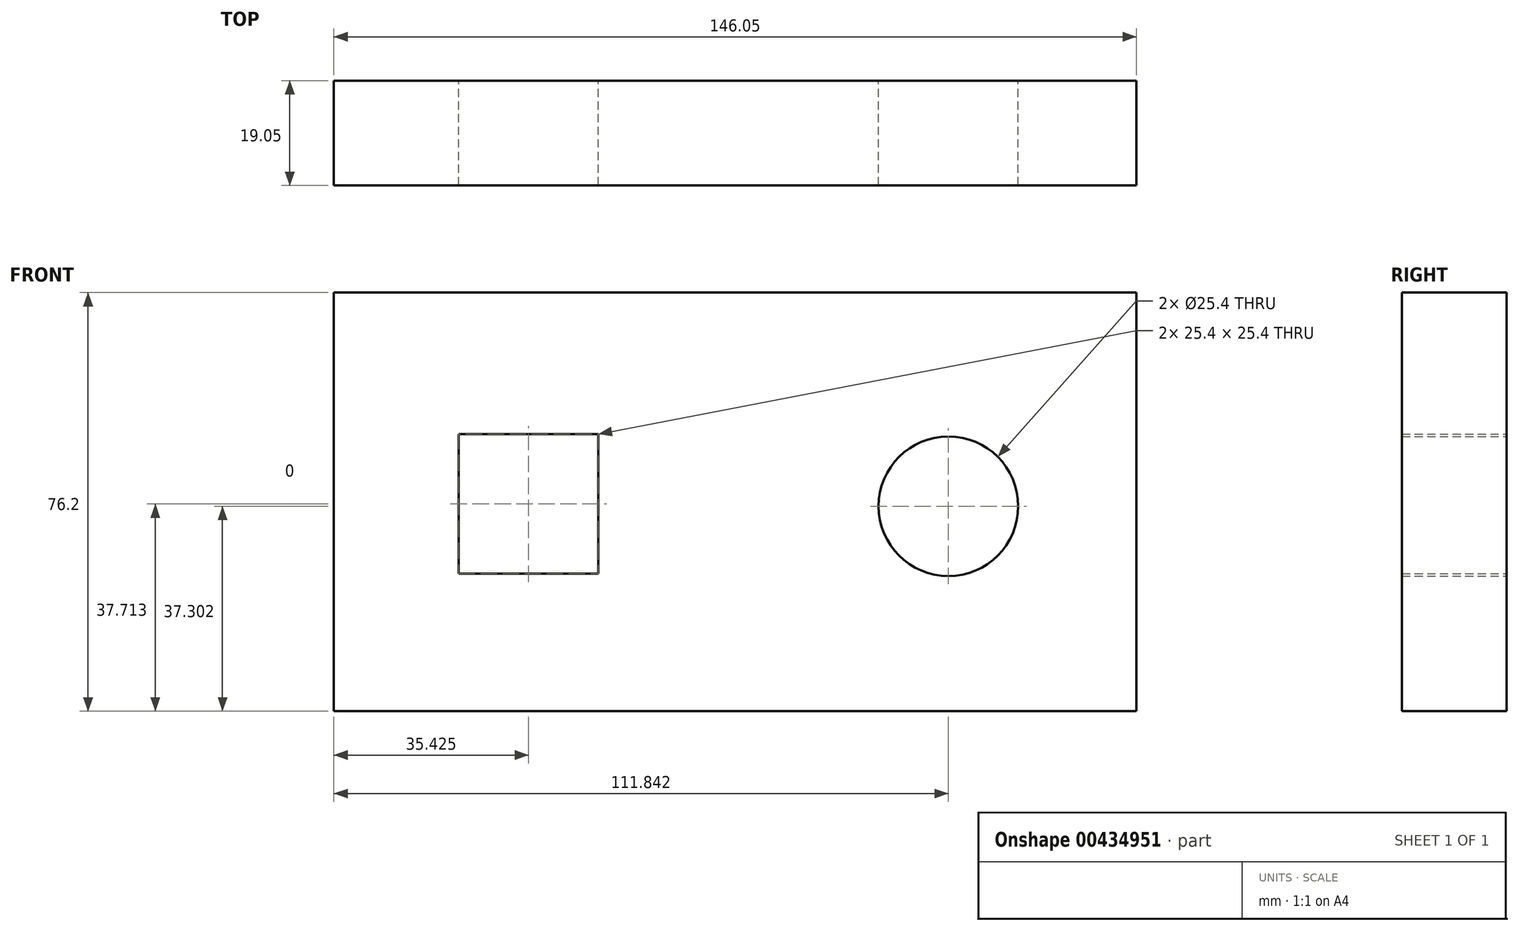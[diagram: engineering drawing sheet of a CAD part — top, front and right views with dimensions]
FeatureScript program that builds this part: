
annotation { "Feature Type Name" : "Feature", "Feature Type Description" : "" }
export const myFeature = defineFeature(function(context is Context, id is Id, definition is map)
    precondition{}
    {
        {
            var Q0;
            Q0=qCreatedBy(makeId("Front.planeOp"),FACE);
            var sketch = newSketch(context, id + "F0", { "sketchPlane" : qUnion([Q0])});
            skLineSegment(sketch, "E0.bottom", {"start": v(-73.14, -28.45) * mm, "end": v(72.91, -28.45) * mm});
            skLineSegment(sketch, "E0.top", {"start": v(-73.14, 47.75) * mm, "end": v(72.91, 47.75) * mm});
            skLineSegment(sketch, "E0.left", {"start": v(-73.14, -28.45) * mm, "end": v(-73.14, 47.75) * mm});
            skLineSegment(sketch, "E0.right", {"start": v(72.91, -28.45) * mm, "end": v(72.91, 47.75) * mm});
            skLineSegment(sketch, "E1.bottom", {"start": v(-50.42, 21.96) * mm, "end": v(-25.02, 21.96) * mm});
            skLineSegment(sketch, "E1.top", {"start": v(-50.42, -3.44) * mm, "end": v(-25.02, -3.44) * mm});
            skLineSegment(sketch, "E1.left", {"start": v(-50.42, 21.96) * mm, "end": v(-50.42, -3.44) * mm});
            skLineSegment(sketch, "E1.right", {"start": v(-25.02, 21.96) * mm, "end": v(-25.02, -3.44) * mm});
            skCircle(sketch, "E2", {"center": v(38.7, 8.85) * mm, "radius": 12.7 * mm});
            skSolve(sketch);
        }
        {
            var Q0;
            Q0=makeQuery(id+"F0.imprint","IMPRINT",FACE,{"disambiguationData":[TD([[makeQuery(id+"F0.imprint","IMPRINT",EDGE,{"derivedFrom":sQuery(id+"F0.wireOp",EDGE,"E0.bottom")}),1.0]])]});
            extrude(context, id + "F1", {"entities" : qUnion([Q0]), "depth" : 19.05 * mm});
        }
    });
